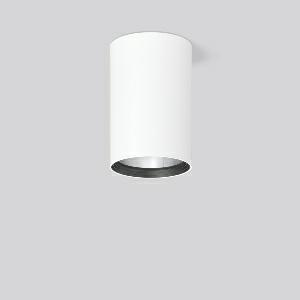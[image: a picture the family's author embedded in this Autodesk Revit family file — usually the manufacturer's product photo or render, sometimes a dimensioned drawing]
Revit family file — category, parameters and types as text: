
# Revit family: heledon_maxi_a_931224_002_1_4435
name_source: partatom
category: Lighting Fixtures
units: mm (PartAtom-declared; Revit-internal decimal feet)

## family parameters
Cut with Voids When Loaded = No
Host = Face
Light Source = No
Part Type = Normal
Room Calculation Point = No
Round Connector Dimension = Use Diameter
Shared = No

## types (1)
- HELEDON maxi A (1 x LED Modul 940, 4550 lm, 4000)
    Apparent Load = 35 VA
    Approval mark = CE
    CIE Flux Codes = 100 100 100 100 100
    Color Rendering = 92
    Color Temperature = 4000
    Default Elevation = 1800 mm
    Description = Series: HELEDON maxi
Cylindrical surface-mounted downlight. Housing: die-cast aluminium, powder-coated. Internal ceiling frame polycarbonate with bayonet mounting. Black plastic ring and recessed LED to prevent glare from the side. Optical assembly with reflector made of MIRO-Silver with 98% total light reflection for outstanding efficiency - can be changed without tools. Best colour rendering index Ra>90. Suitable for Ceiling mounting. Easy installation with a separate ceiling frame with bayonet mounting and plug connection. Driver integrated. Connected via plug-in connector. High quality converter without flickering and stroboscopic effect. The following accessories can be mounted without use of tools: interchangeable lenses, decorative glasses, honeycomb louvre, clear and frosted diffusers, white interchangeable plastic ring. 
Colour: traffic white, matt (RAL 9016)
Diameter: 123 mm
Height: 183 mm
Lamp: LED
Socket: without socket
Colour temperature: 4000K
Colour rendering index (CRI): 92
System power: 35 W
Rated luminous flux: 4550 lm
Luminous efficiency: 130 lm/W
Control gear: Regulated power supply
Protection class: I
Type of protection: IP 20
    Height = 183 mm
    Lamp = 1 x LED Modul 940
    Lamp Light Flux = 4550 lm
    Lamp count = 1
    Length = 123 mm
    Lifetime = 50000 h
    Luminous efficacy = 130 lm/W
    Manufacturer = RZB
    ModVariant = No
    Model = 931224.002.1
    Mounting Place = Ceiling
    Mounting Type = Surface mounted
    Number of Poles = 1
    OnlyDefault = Yes
    Power Factor = 1
    Product Name = HELEDON maxi A
    Product group = Surface mounted downlights
    ProductGroupID = 302
    Protection Class = Protection class I
    Protection Degree = IP 20
    RLX_Detail_Level = 1
    RLX_Emergency_Light_Flux = 0 lm
    RLX_Emergency_Type = 0
    RLX_Emergency_Type_DB = No
    RlxData = <blob elided: 98145 chars, md5=fab6fc1d>
    Socket = socket
    Standby Power = 0 W
    System Light Flux = 4550 lm
    System Power = 35 W
    Type Comments = Product without accessories
    Type Image = 931192.002.jpg
    URL = http://relux.com
    VarID = ---
    Voltage = 230 V
    Voltage Range = 220-240 V
    Weight = 0.00 kg
    Width = 0 mm  [stored 0 ft]

note: [stored X ft] marks values corroborated as IEEE doubles in the binary element streams (Revit-internal decimal feet)

## geometry (parser evidence)
native form markers: Blend x4, Sweep x11
no freeform markers — native parametric forms only
